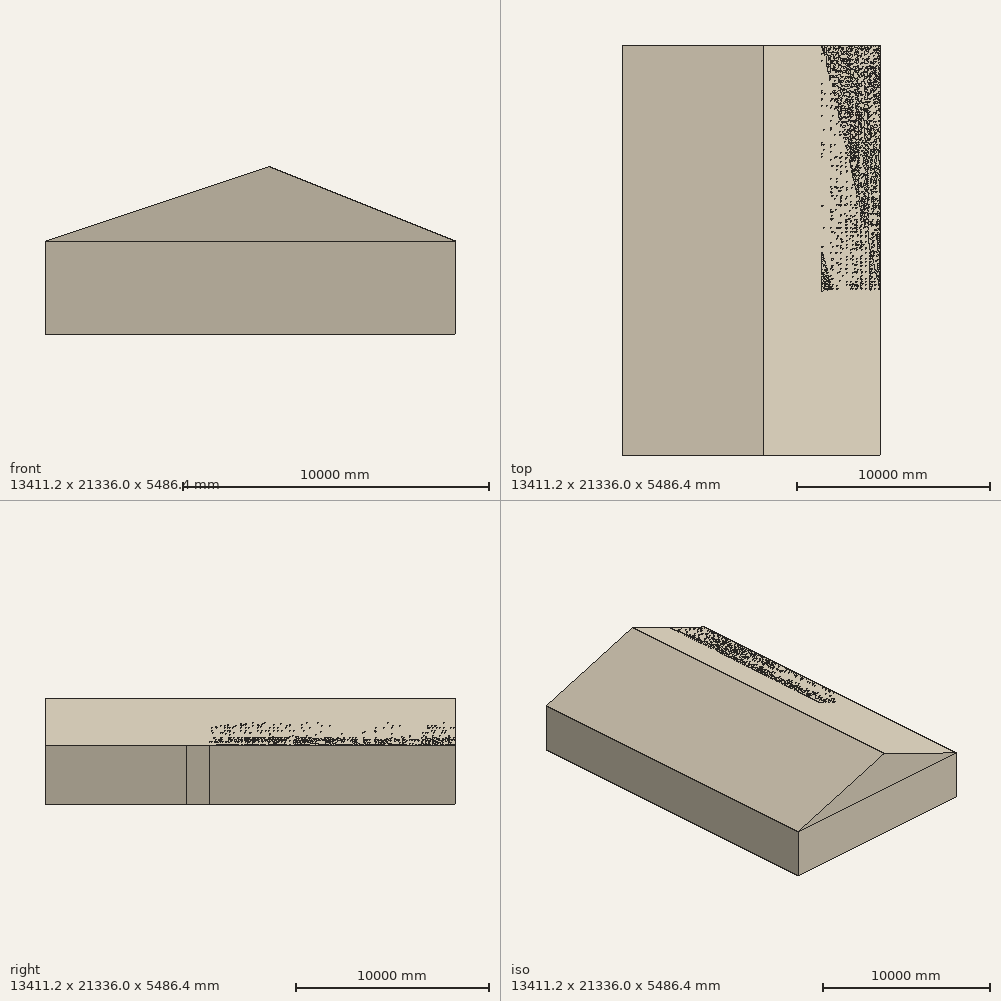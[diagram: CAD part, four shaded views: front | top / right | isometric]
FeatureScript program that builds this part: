
annotation { "Feature Type Name" : "Feature", "Feature Type Description" : "" }
export const myFeature = defineFeature(function(context is Context, id is Id, definition is map)
    precondition{}
    {
        {
            var Q0;
            Q0=qCreatedBy(makeId("Front.planeOp"),FACE);
            var sketch = newSketch(context, id + "F0", { "sketchPlane" : qUnion([Q0])});
            skLineSegment(sketch, "E0.bottom", {"start": v(0, 0) * mm, "end": v(13411.2, 0) * mm});
            skLineSegment(sketch, "E0.top", {"start": v(0, 3048) * mm, "end": v(13411.2, 3048) * mm});
            skLineSegment(sketch, "E0.left", {"start": v(0, 0) * mm, "end": v(0, 3048) * mm});
            skLineSegment(sketch, "E0.right", {"start": v(13411.2, 0) * mm, "end": v(13411.2, 3048) * mm});
            skLineSegment(sketch, "E1.0", {"start": v(152.4, 2895.6) * mm, "end": v(13258.8, 2895.6) * mm});
            skLineSegment(sketch, "E1.1", {"start": v(152.4, 152.4) * mm, "end": v(152.4, 2895.6) * mm});
            skLineSegment(sketch, "E1.2", {"start": v(152.4, 152.4) * mm, "end": v(13258.8, 152.4) * mm});
            skLineSegment(sketch, "E1.3", {"start": v(13258.8, 152.4) * mm, "end": v(13258.8, 2895.6) * mm});
            skSolve(sketch);
        }
        {
            var Q0;
            Q0=makeQuery(id+"F0.imprint","IMPRINT",FACE,{"disambiguationData":[TD([[makeQuery(id+"F0.imprint","IMPRINT",EDGE,{"derivedFrom":sQuery(id+"F0.wireOp",EDGE,"E0.bottom")}),1.0]])]});
            var Q1;
            Q1=makeQuery(id+"F0.imprint","IMPRINT",FACE,{"disambiguationData":[TD([[makeQuery(id+"F0.imprint","IMPRINT",EDGE,{"derivedFrom":sQuery(id+"F0.wireOp",EDGE,"E1.0")}),-1.0]])]});
            extrude(context, id + "F1", {"entities" : qUnion([Q0, Q1]), "oppositeDirection" : true, "depth" : 7315.2 * mm, "offsetDistance" : 25.4 * mm});
        }
        {
            var Q0;
            Q0=makeQuery(id+"F1.opExtrude","CAP_FACE",FACE,{"disambiguationData":[OSD([sQuery(id+"F0.wireOp",EDGE,"E0.bottom"),sQuery(id+"F0.wireOp",EDGE,"E0.top"),sQuery(id+"F0.wireOp",EDGE,"E0.left"),sQuery(id+"F0.wireOp",EDGE,"E0.right")])],"isStart":false});
            cPlane(context, id + "F2", {"entities" : qUnion([Q0]), "cplaneType" : CPlaneType.OFFSET, "offset" : 1219.2 * mm, "width" : 152.4 * mm, "height" : 152.4 * mm});
        }
        {
            var Q0;
            Q0=qCreatedBy(id+"F2.planeOp",FACE);
            var sketch = newSketch(context, id + "F3", { "sketchPlane" : qUnion([Q0])});
            skLineSegment(sketch, "E2.0", {"start": v(-13411.2, 0) * mm, "end": v(-13411.2, 3048) * mm});
            skLineSegment(sketch, "E3", {"start": v(-13411.2, 3048) * mm, "end": v(-7315.2, 3048) * mm});
            skLineSegment(sketch, "E4", {"start": v(-3657.6, 0) * mm, "end": v(-13411.2, 0) * mm});
            skLineSegment(sketch, "E5.right", {"start": v(-3657.6, 0) * mm, "end": v(-3657.6, 2438.4) * mm});
            skLineSegment(sketch, "E6", {"start": v(-7315.2, 3048) * mm, "end": v(-3657.6, 2438.4) * mm});
            skSolve(sketch);
        }
        {
            var Q0;
            Q0=makeQuery(id+"F3.imprint","IMPRINT",FACE,{"disambiguationData":[TD([[makeQuery(id+"F3.imprint","IMPRINT",EDGE,{"derivedFrom":sQuery(id+"F3.wireOp",EDGE,"E2.0")}),-1.0]])]});
            var Q1;
            {var subQ0=makeQuery(id+"F1.opExtrude","CAP_EDGE",EDGE,{"disambiguationData":[OSD([sQuery(id+"F0.wireOp",EDGE,"E1.3")])],"isStart":false});Q1=makeQuery(id+"F3.imprint","IMPRINT",FACE,{"disambiguationData":[TD([[makeQuery(id+"F3.imprint","IMPRINT",EDGE,{"derivedFrom":subQ0}),-1.0]])]});}
            extrude(context, id + "F4", {"entities" : qUnion([Q0, Q1]), "depth" : 12801.6 * mm, "offsetDistance" : 25.4 * mm});
        }
        {
            var Q0;
            Q0=makeQuery(id+"F4.opExtrude","CAP_FACE",FACE,{"disambiguationData":[OSD([sQuery(id+"F3.wireOp",EDGE,"E2.0"),sQuery(id+"F3.wireOp",EDGE,"E3"),sQuery(id+"F3.wireOp",EDGE,"E4"),sQuery(id+"F3.wireOp",EDGE,"E5.right"),sQuery(id+"F3.wireOp",EDGE,"E6")])],"isStart":true});
            var sketch = newSketch(context, id + "F5", { "sketchPlane" : qUnion([Q0])});
            skLineSegment(sketch, "E7", {"start": v(10363.2, 3048) * mm, "end": v(10363.2, 4267.2) * mm});
            skLineSegment(sketch, "E8", {"start": v(7315.2, 3048) * mm, "end": v(10363.2, 4267.2) * mm});
            skLineSegment(sketch, "E9", {"start": v(10363.2, 4267.2) * mm, "end": v(13411.2, 3048) * mm});
            skSolve(sketch);
        }
        {
            var Q0;
            {var subQ0=sQuery(id+"F5.wireOp",EDGE,"E7");Q0=makeQuery(id+"F5.imprint","IMPRINT",FACE,{"disambiguationData":[TD([[makeQuery(id+"F5.imprint","IMPRINT",EDGE,{"derivedFrom":subQ0}),1.0]])]});}
            var Q1;
            {var subQ0=sQuery(id+"F5.wireOp",EDGE,"E7");Q1=makeQuery(id+"F5.imprint","IMPRINT",FACE,{"disambiguationData":[TD([[makeQuery(id+"F5.imprint","IMPRINT",EDGE,{"derivedFrom":subQ0}),-1.0]])]});}
            var Q2;
            Q2=makeQuery(id+"F4.opExtrude","CAP_FACE",FACE,{"disambiguationData":[OSD([sQuery(id+"F3.wireOp",EDGE,"E2.0"),sQuery(id+"F3.wireOp",EDGE,"E3"),sQuery(id+"F3.wireOp",EDGE,"E4"),sQuery(id+"F3.wireOp",EDGE,"E5.right"),sQuery(id+"F3.wireOp",EDGE,"E6")])],"isStart":false});
            extrude(context, id + "F6", {"entities" : qUnion([Q0, Q1]), "operationType" : NewBodyOperationType.ADD, "endBound" : BoundingType.UP_TO_SURFACE, "oppositeDirection" : true, "depth" : 25.4 * mm, "endBoundEntityFace" : qUnion([Q2]), "offsetDistance" : 25.4 * mm});
        }
        {
            var Q0;
            Q0=makeQuery(id+"F1.opExtrude","CAP_FACE",FACE,{"disambiguationData":[OSD([sQuery(id+"F0.wireOp",EDGE,"E0.bottom"),sQuery(id+"F0.wireOp",EDGE,"E0.top"),sQuery(id+"F0.wireOp",EDGE,"E0.left"),sQuery(id+"F0.wireOp",EDGE,"E0.right")])],"isStart":false});
            var sketch = newSketch(context, id + "F7", { "sketchPlane" : qUnion([Q0])});
            skLineSegment(sketch, "E10.0", {"start": v(-3657.6, 0) * mm, "end": v(-3657.6, 3048) * mm});
            skLineSegment(sketch, "E11", {"start": v(-3657.6, 3048) * mm, "end": v(0, 3048) * mm});
            skLineSegment(sketch, "E12", {"start": v(0, 3048) * mm, "end": v(0, 0) * mm});
            skLineSegment(sketch, "E13", {"start": v(0, 0) * mm, "end": v(-3657.6, 0) * mm});
            skSolve(sketch);
        }
        {
            var Q0;
            Q0=makeQuery(id+"F7.imprint","IMPRINT",FACE,{"disambiguationData":[TD([[makeQuery(id+"F7.imprint","IMPRINT",EDGE,{"derivedFrom":sQuery(id+"F7.wireOp",EDGE,"E10.0")}),-1.0]])]});
            var Q1;
            {var subQ0=sQuery(id+"F3.wireOp",EDGE,"E3");Q1=makeQuery(id+"F6.boolean.opBoolean","MERGE",FACE,{"derivedFrom":[makeQuery(id+"F4.opExtrude","CAP_FACE",FACE,{"disambiguationData":[OSD([sQuery(id+"F3.wireOp",EDGE,"E2.0"),subQ0,sQuery(id+"F3.wireOp",EDGE,"E4"),sQuery(id+"F3.wireOp",EDGE,"E5.right"),sQuery(id+"F3.wireOp",EDGE,"E6")])],"isStart":false}),makeQuery(id+"F6.opExtrude","CAP_FACE",FACE,{"disambiguationData":[OSD([subQ0,sQuery(id+"F5.wireOp",EDGE,"E8"),sQuery(id+"F5.wireOp",EDGE,"E9")])],"isStart":false})]});}
            extrude(context, id + "F8", {"entities" : qUnion([Q0]), "operationType" : NewBodyOperationType.ADD, "endBound" : BoundingType.UP_TO_SURFACE, "depth" : 25.4 * mm, "endBoundEntityFace" : qUnion([Q1]), "offsetDistance" : 25.4 * mm});
        }
        {
            var Q0;
            Q0=makeQuery(id+"F1.opExtrude","CAP_FACE",FACE,{"disambiguationData":[OSD([sQuery(id+"F0.wireOp",EDGE,"E0.bottom"),sQuery(id+"F0.wireOp",EDGE,"E0.top"),sQuery(id+"F0.wireOp",EDGE,"E0.left"),sQuery(id+"F0.wireOp",EDGE,"E0.right")])],"isStart":true});
            var sketch = newSketch(context, id + "F9", { "sketchPlane" : qUnion([Q0])});
            skLineSegment(sketch, "E14", {"start": v(7315.2, 3048) * mm, "end": v(7315.2, 5486.4) * mm});
            skLineSegment(sketch, "E15", {"start": v(7315.2, 5486.4) * mm, "end": v(13411.2, 3048) * mm});
            skLineSegment(sketch, "E16", {"start": v(13411.2, 3048) * mm, "end": v(0, 3048) * mm});
            skLineSegment(sketch, "E17", {"start": v(0, 3048) * mm, "end": v(7315.2, 5486.4) * mm});
            skSolve(sketch);
        }
        {
            var Q0;
            {var subQ0=sQuery(id+"F9.wireOp",EDGE,"E14");Q0=makeQuery(id+"F9.imprint","IMPRINT",FACE,{"disambiguationData":[TD([[makeQuery(id+"F9.imprint","IMPRINT",EDGE,{"derivedFrom":subQ0}),1.0]])]});}
            var Q1;
            {var subQ0=sQuery(id+"F9.wireOp",EDGE,"E14");Q1=makeQuery(id+"F9.imprint","IMPRINT",FACE,{"disambiguationData":[TD([[makeQuery(id+"F9.imprint","IMPRINT",EDGE,{"derivedFrom":subQ0}),-1.0]])]});}
            var Q2;
            {var subQ0=sQuery(id+"F3.wireOp",EDGE,"E3");Q2=makeQuery(id+"F6.boolean.opBoolean","MERGE",FACE,{"derivedFrom":[makeQuery(id+"F4.opExtrude","CAP_FACE",FACE,{"disambiguationData":[OSD([sQuery(id+"F3.wireOp",EDGE,"E2.0"),subQ0,sQuery(id+"F3.wireOp",EDGE,"E4"),sQuery(id+"F3.wireOp",EDGE,"E5.right"),sQuery(id+"F3.wireOp",EDGE,"E6")])],"isStart":false}),makeQuery(id+"F6.opExtrude","CAP_FACE",FACE,{"disambiguationData":[OSD([subQ0,sQuery(id+"F5.wireOp",EDGE,"E8"),sQuery(id+"F5.wireOp",EDGE,"E9")])],"isStart":false})]});}
            extrude(context, id + "F10", {"entities" : qUnion([Q0, Q1]), "endBound" : BoundingType.UP_TO_SURFACE, "oppositeDirection" : true, "depth" : 25.4 * mm, "endBoundEntityFace" : qUnion([Q2]), "offsetDistance" : 25.4 * mm});
        }
    });
